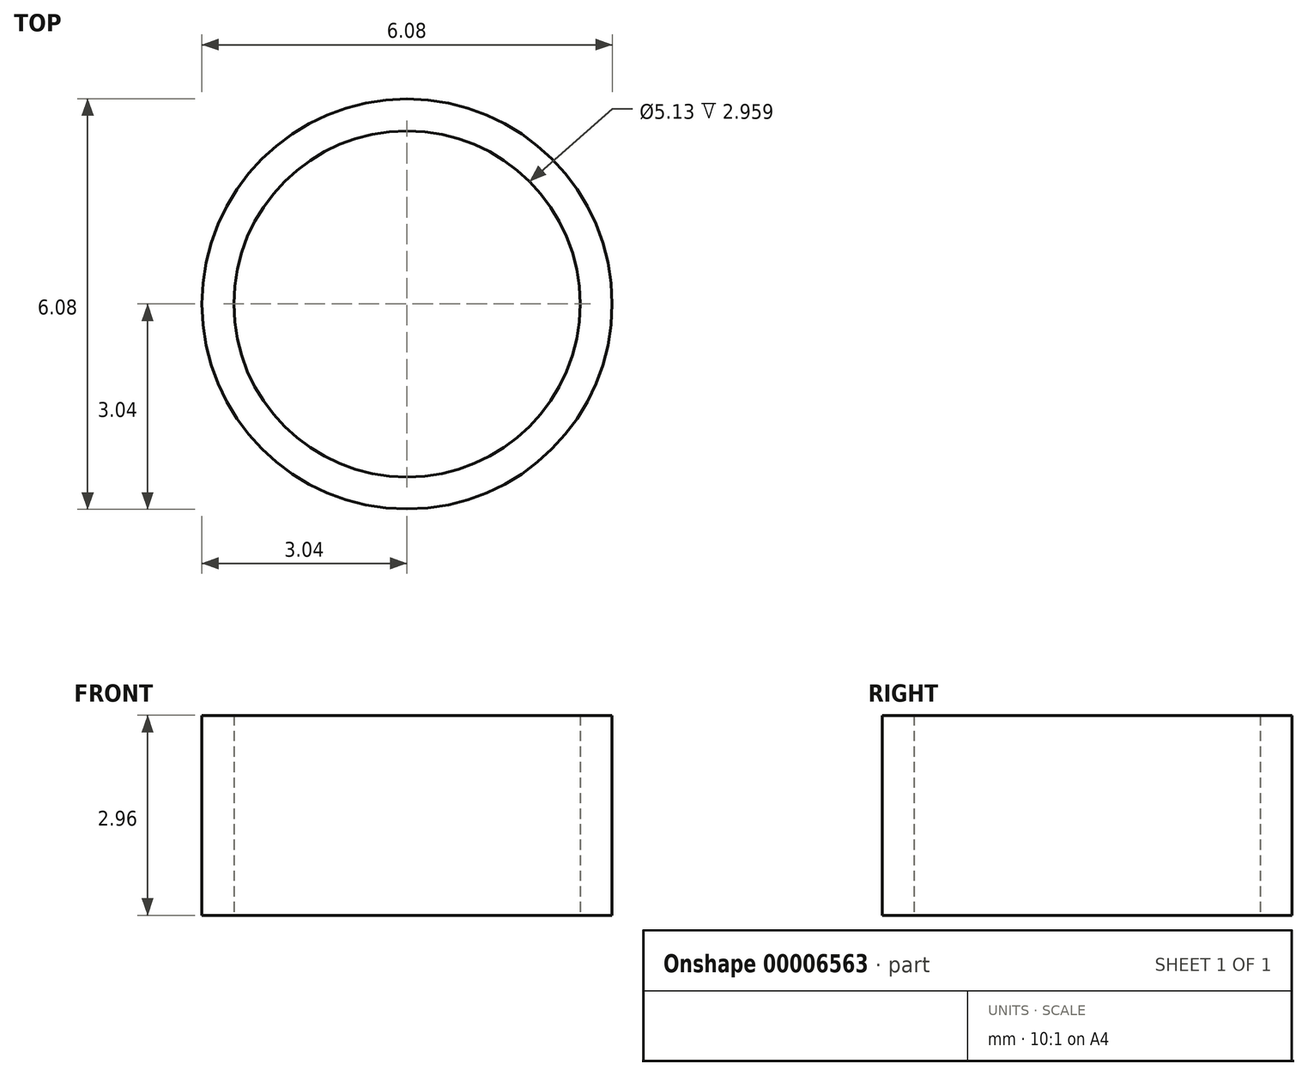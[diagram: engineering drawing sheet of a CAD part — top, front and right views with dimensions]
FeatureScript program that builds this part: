
annotation { "Feature Type Name" : "Feature", "Feature Type Description" : "" }
export const myFeature = defineFeature(function(context is Context, id is Id, definition is map)
    precondition{}
    {
        {
            var Q0;
            Q0=qCreatedBy(makeId("Top.planeOp"),FACE);
            var sketch = newSketch(context, id + "F0", { "sketchPlane" : qUnion([Q0])});
            skCircle(sketch, "E0", {"center": v(0, 0) * mm, "radius": 2.56 * mm});
            skCircle(sketch, "E1", {"center": v(0, 0) * mm, "radius": 3.04 * mm});
            skSolve(sketch);
        }
        {
            var Q0;
            Q0=makeQuery(id+"F0.imprint","IMPRINT",FACE,{"disambiguationData":[TD([[makeQuery(id+"F0.imprint","IMPRINT",EDGE,{"derivedFrom":sQuery(id+"F0.wireOp",EDGE,"E0")}),-1.0]])]});
            extrude(context, id + "F1", {"entities" : qUnion([Q0]), "depth" : 2.96 * mm});
        }
    });
